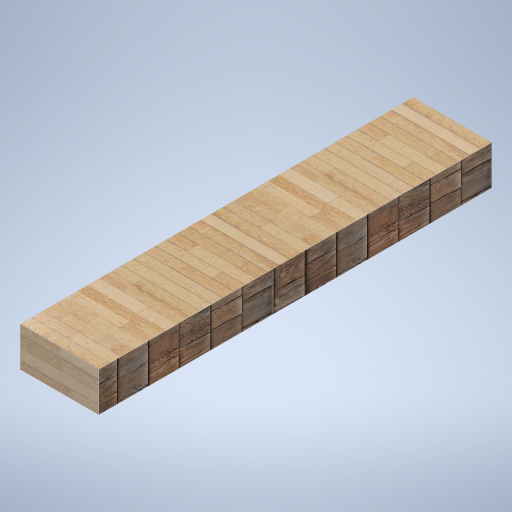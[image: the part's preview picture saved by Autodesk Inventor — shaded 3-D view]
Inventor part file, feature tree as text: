
AUTODESK INVENTOR PART (.ipt)
format: ipt  version: 2024.2 (Build 282272000, 272)  size: 371,712 bytes
history: native  units: mm
features: extrude x1, sketch x1
ambient origin geometry x8: Origin, YZ Plane, XZ Plane, XY Plane, X Axis, Y Axis, Z Axis, Center Point
bodies: Solid1 (feature_tree)
feature tree (2):
  extrude  "Extrusion1"  Depth=200.0mm
  sketch  "Sketch1"  dims[d0=400.0mm d1=200.0mm d2=2000.0mm d3=0.0mm]
